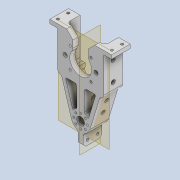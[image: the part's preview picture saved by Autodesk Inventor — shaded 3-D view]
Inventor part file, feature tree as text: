
AUTODESK INVENTOR PART (.ipt)
format: ipt  version: 2020 (Build 240168000, 168)  size: 657,920 bytes
history: native  units: mm
features: extrude x20, sketch x20, projected_geometry x16, fillet x13, thicken_offset x4, other x4, chamfer x3, mirror x3, plane x2, pattern_circular x2, reference x2
ambient origin geometry x8: Origin, YZ Plane, XZ Plane, XY Plane, X Axis, Y Axis, Z Axis, Center Point
bodies: Solid1 (feature_tree)
feature tree (89):
  extrude  "Extrusion1"  Depth=15.0mm
  extrude  "Extrusion2"  Depth=30.0mm
  extrude  "Extrusion3"  Depth=6.0mm
  extrude  "Extrusion4"  Depth=4.0mm TaperAngle=0.0deg
  extrude  "Extrusion5"  Depth=4.0mm TaperAngle=0.0deg
  extrude  "Extrusion6"  Depth=3.0mm
  extrude  "Extrusion7"  Depth=4.0mm
  plane  "Work Plane1"
  extrude  "Extrusion8"  Depth=4.0mm
  chamfer  "Chamfer1"  Distance=10.5mm
  extrude  "Extrusion9"  Depth=30.0mm
  pattern_circular  "Circular Pattern1"  Count=2  [1 undecoded]
  thicken_offset  "Thicken1"
  fillet  "Fillet1"  Radius=80.0mm
  fillet  "Fillet2"  Radius=4.0mm
  extrude  "Extrusion10"  Depth=4.0mm
  pattern_circular  "Circular Pattern2"  [2 undecoded]
  extrude  "Extrusion11"  Depth=4.0mm
  extrude  "Extrusion12"  Depth=4.0mm
  extrude  "Extrusion13"  Depth=10.0mm TaperAngle=0.0deg
  extrude  "Extrusion14"  Depth=4.0mm TaperAngle=360.0deg
  extrude  "Extrusion15"  Depth=10.0mm TaperAngle=0.0deg
  plane  "Work Plane2"
  mirror  "Mirror1"
  extrude  "Extrusion16"  Depth=4.0mm
  extrude  "Extrusion17"  Depth=12.0mm
  mirror  "Mirror2"
  extrude  "Extrusion18"  Depth=10.0mm TaperAngle=0.0deg
  mirror  "Mirror3"
  extrude  "Extrusion19"  Depth=4.0mm
  thicken_offset  "Thicken2"
  extrude  "Extrusion20"  Depth=4.0mm
  fillet  "Fillet3"  Radius=12.0mm
  fillet  "Fillet4"  Radius=10.0mm
  fillet  "Fillet5"  Radius=6.0mm
  fillet  "Fillet6"  Radius=7.0mm
  fillet  "Fillet7"  Radius=5.0mm
  fillet  "Fillet8"  Radius=10.0mm
  chamfer  "Chamfer2"  Distance=10.0mm
  fillet  "Fillet9"  Radius=10.0mm
  thicken_offset  "Thicken3"
  thicken_offset  "Thicken4"
  fillet  "Fillet10"  Radius=3.2mm
  fillet  "Fillet11"  Radius=3.2mm
  fillet  "Fillet12"  Radius=10.0mm
  fillet  "Fillet13"  Radius=6.0mm
  chamfer  "Chamfer3"  Distance=14.5mm
  sketch  "Sketch1"  dims[d0=38.7mm d1=15.0mm]
  reference  "Reference1"
  sketch  "Sketch2"  dims[d2=30.0mm d3=30.0mm]
  sketch  "Sketch3"  dims[d4=19.35mm d5=6.0mm]
  projected_geometry  "Projected Loop1"
  sketch  "Sketch4"  dims[d6=38.7mm d7=4.0mm d8=0.0mm]
  projected_geometry  "Projected Loop2"
  sketch  "Sketch5"  dims[d9=17.0mm d10=4.0mm d11=0.0mm]
  projected_geometry  "Projected Loop3"
  sketch  "Sketch6"  dims[d12=3.0mm d13=3.0mm]
  projected_geometry  "Projected Loop4"
  sketch  "Sketch7"  dims[d14=4.0mm d15=0.0mm d16=4.0mm]
  projected_geometry  "Projected Loop5"
  sketch  "Sketch8"  dims[d17=5.0mm d18=4.0mm]
  sketch  "Sketch9"  dims[d19=5.0mm d20=10.5mm d21=0.0mm]
  projected_geometry  "Projected Loop6"
  sketch  "Sketch10"  dims[d22=14.5mm d23=30.0mm]
  projected_geometry  "Projected Loop7"
  sketch  "Sketch11"  dims[d24=3.0mm d25=0.0mm]
  projected_geometry  "Projected Loop8"
  sketch  "Sketch12"  dims[d26=3.0mm d27=0.0mm]
  reference  "Reference2"
  sketch  "Sketch13"  dims[d28=6.15mm]
  projected_geometry  "Projected Loop9"
  sketch  "Sketch14"  dims[d29=3.0mm d30=0.0mm]
  projected_geometry  "Projected Loop10"
  sketch  "Sketch15"  dims[d31=-2.5mm]
  projected_geometry  "Projected Loop11"
  sketch  "Sketch16"  dims[d32=1.0mm]
  projected_geometry  "Projected Loop12"
  projected_geometry  "Projected Loop13"
  sketch  "Sketch17"  dims[d33=9.0mm d34=0.0mm]
  projected_geometry  "Projected Loop14"
  sketch  "Sketch18"  dims[d35=1.0mm d36=2.0mm d37=45.0deg]
  projected_geometry  "Projected Loop15"
  sketch  "Sketch19"  dims[d38=1.5mm d39=20.0mm d40=0.0mm d41=80.0mm d42=360.0deg d44=4.0mm]
  projected_geometry  "Projected Loop16"
  sketch  "Sketch20"  dims[d45=4.0mm d46=5.0mm d47=3.0mm d48=11.5mm d49=1.8mm d50=10.0mm d51=0.0mm d52=40.0mm d53=360.0deg d55=10.0mm d56=0.0mm d57=20.0mm d58=12.0mm d59=10.0mm d60=0.0mm d61=13.0mm d62=4.0mm d63=12.0mm d64=10.0mm d65=0.0mm d66=6.0mm d67=7.0mm d68=5.0mm d69=10.0mm d70=0.0mm d71=10.0mm d72=10.0mm d73=3.2mm d74=3.2mm d75=10.0mm d76=0.0mm d77=6.0mm d78=14.5mm d79=6.0mm d80=14.5mm d81=3.0mm d82=0.0mm d83=4.0mm d84=4.0mm d85=2.0mm d86=2.0mm d87=3.0mm d88=0.0mm d89=7.0mm d90=15.0mm d91=3.2mm d92=3.2mm d93=3.0mm d94=0.0mm d95=4.0mm d96=2.0mm d97=4.0mm d98=2.0mm d99=4.0mm d100=0.0mm d101=2.0mm d102=2.0mm d103=12.0mm d104=3.2mm d105=12.0mm d106=3.2mm d107=4.0mm d108=0.0mm d109=5.0mm d110=0.5mm d111=1.0mm d112=1.0mm d113=3.0mm d114=2.0mm d115=2.0mm d116=2.0mm d117=45.0deg d118=2.0mm d119=2.0mm d120=2.0mm d121=2.0mm d122=2.0mm d123=1.5mm d124=2.0mm d125=3.0mm d126=4.0mm d127=5.0mm d128=2.0mm d129=45.0deg]
  parser-record x1  (decoder bookkeeping rows leaked as tree rows — omitted from the tree; the rows remain in map.json)
  other  "reducer_unit.iam"
  other  "mot_27_ass:1"
  other  "mot_27_2:1"
note: 3 required parameter values undecoded (feature->parameter linkage not recoverable at this tier; creation-order binding heuristic only, values carry confidence <= 0.55)
note: 1 file-system path scrubbed to <path> (originals preserved in map.json)
